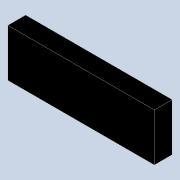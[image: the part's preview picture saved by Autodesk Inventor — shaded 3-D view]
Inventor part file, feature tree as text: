
AUTODESK INVENTOR PART (.ipt)
format: ipt  version: 2021 (Build 250183000, 183)  size: 76,288 bytes
history: native  units: in
note: dims shown in document units (in); Inventor stores cm internally (conversion verified against a paired STEP export)
features: extrude x1, sketch x1
ambient origin geometry x8: Origin, YZ Plane, XZ Plane, XY Plane, X Axis, Y Axis, Z Axis, Center Point
bodies: Solid1 (feature_tree)
feature tree (2):
  extrude  "Extrusion1"  Depth=3.8438in
  sketch  "Sketch1"  dims[d0=0.4688in d1=3.8438in d2=1.25in d3=0.0in]
